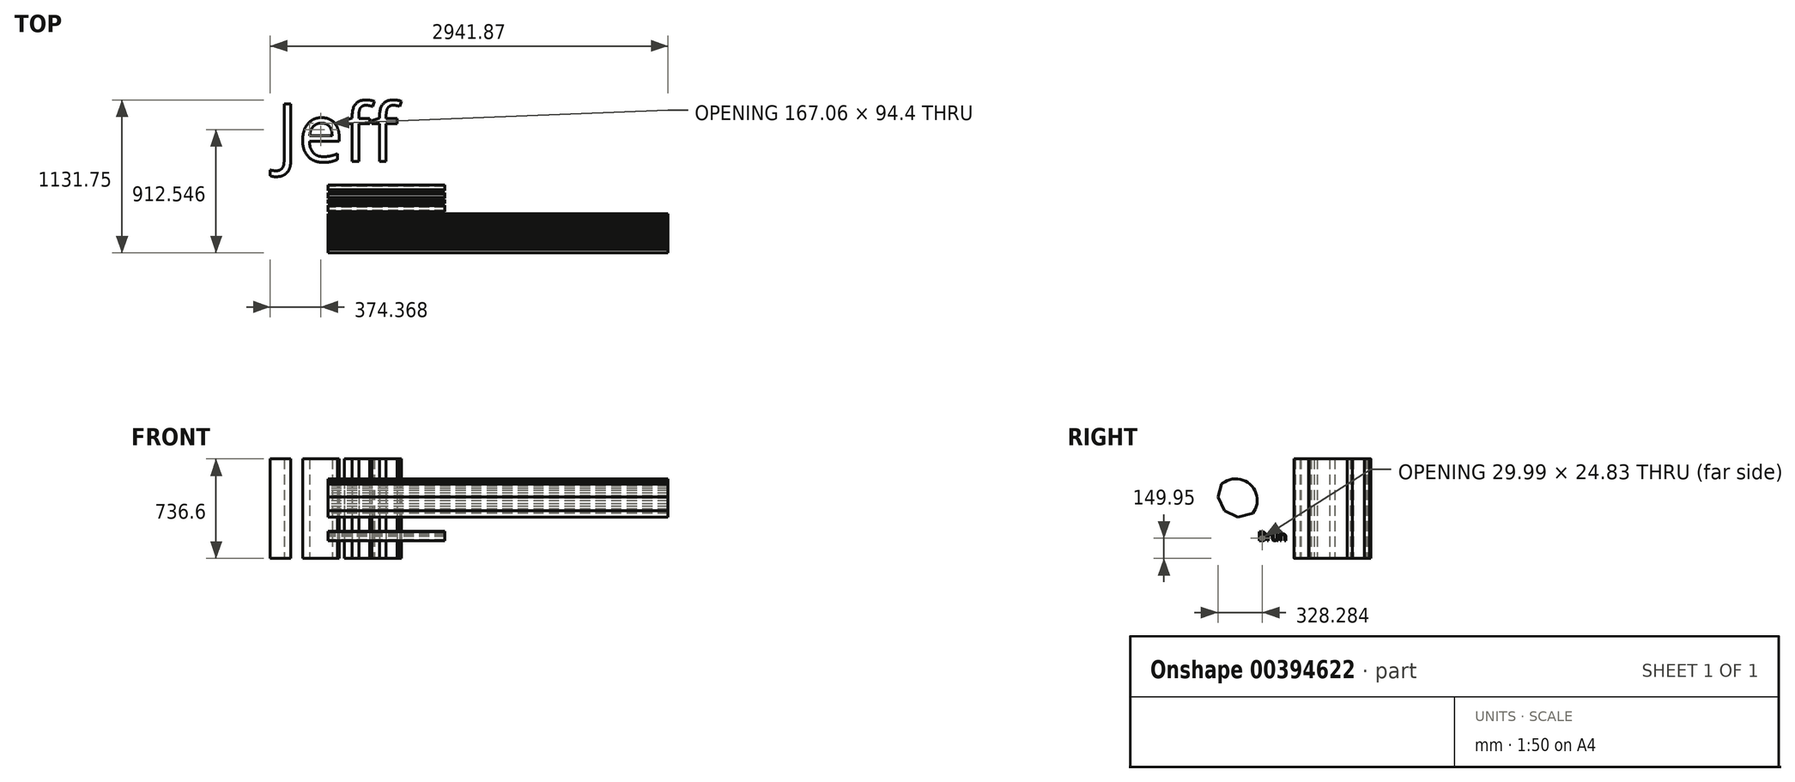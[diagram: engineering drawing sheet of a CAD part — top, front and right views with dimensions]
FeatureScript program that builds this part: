
annotation { "Feature Type Name" : "Feature", "Feature Type Description" : "" }
export const myFeature = defineFeature(function(context is Context, id is Id, definition is map)
    precondition{}
    {
        {
            var Q0;
            Q0=qCreatedBy(makeId("Right.planeOp"),FACE);
            var sketch = newSketch(context, id + "F0", { "sketchPlane" : qUnion([Q0])});
            skCircle(sketch, "E0.cCircle", {"center": v(-776.3, 430.45) * mm, "radius": 159.13 * mm, "construction": true});
            skLineSegment(sketch, "E0.0", {"start": v(-918.13, 358.3) * mm, "end": v(-926.05, 376.64) * mm});
            skLineSegment(sketch, "E0.1", {"start": v(-926.05, 376.64) * mm, "end": v(-931.62, 395.83) * mm});
            skLineSegment(sketch, "E0.2", {"start": v(-931.62, 395.83) * mm, "end": v(-934.73, 415.57) * mm});
            skLineSegment(sketch, "E0.3", {"start": v(-934.73, 415.57) * mm, "end": v(-935.35, 435.54) * mm});
            skLineSegment(sketch, "E0.4", {"start": v(-935.35, 435.54) * mm, "end": v(-933.45, 455.44) * mm});
            skLineSegment(sketch, "E0.5", {"start": v(-933.45, 455.44) * mm, "end": v(-929.08, 474.94) * mm});
            skLineSegment(sketch, "E0.6", {"start": v(-929.08, 474.94) * mm, "end": v(-922.3, 493.73) * mm});
            skLineSegment(sketch, "E0.7", {"start": v(-922.3, 493.73) * mm, "end": v(-913.22, 511.53) * mm});
            skLineSegment(sketch, "E0.8", {"start": v(-913.22, 511.53) * mm, "end": v(-901.98, 528.05) * mm});
            skLineSegment(sketch, "E0.9", {"start": v(-901.98, 528.05) * mm, "end": v(-888.75, 543.04) * mm});
            skLineSegment(sketch, "E0.10", {"start": v(-888.75, 543.04) * mm, "end": v(-873.76, 556.24) * mm});
            skLineSegment(sketch, "E0.11", {"start": v(-873.76, 556.24) * mm, "end": v(-857.22, 567.46) * mm});
            skLineSegment(sketch, "E0.12", {"start": v(-857.22, 567.46) * mm, "end": v(-839.41, 576.53) * mm});
            skLineSegment(sketch, "E0.13", {"start": v(-839.41, 576.53) * mm, "end": v(-820.6, 583.28) * mm});
            skLineSegment(sketch, "E0.14", {"start": v(-820.6, 583.28) * mm, "end": v(-801.1, 587.63) * mm});
            skLineSegment(sketch, "E0.15", {"start": v(-801.1, 587.63) * mm, "end": v(-781.2, 589.5) * mm});
            skLineSegment(sketch, "E0.16", {"start": v(-781.2, 589.5) * mm, "end": v(-761.23, 588.86) * mm});
            skLineSegment(sketch, "E0.17", {"start": v(-761.23, 588.86) * mm, "end": v(-741.5, 585.72) * mm});
            skLineSegment(sketch, "E0.18", {"start": v(-741.5, 585.72) * mm, "end": v(-722.31, 580.14) * mm});
            skLineSegment(sketch, "E0.19", {"start": v(-722.31, 580.14) * mm, "end": v(-703.98, 572.19) * mm});
            skLineSegment(sketch, "E0.20", {"start": v(-703.98, 572.19) * mm, "end": v(-686.78, 562) * mm});
            skLineSegment(sketch, "E0.21", {"start": v(-686.78, 562) * mm, "end": v(-671, 549.75) * mm});
            skLineSegment(sketch, "E0.22", {"start": v(-671, 549.75) * mm, "end": v(-656.88, 535.61) * mm});
            skLineSegment(sketch, "E0.23", {"start": v(-656.88, 535.61) * mm, "end": v(-644.64, 519.81) * mm});
            skLineSegment(sketch, "E0.24", {"start": v(-644.64, 519.81) * mm, "end": v(-634.48, 502.6) * mm});
            skLineSegment(sketch, "E0.25", {"start": v(-634.48, 502.6) * mm, "end": v(-626.55, 484.26) * mm});
            skLineSegment(sketch, "E0.26", {"start": v(-626.55, 484.26) * mm, "end": v(-620.99, 465.07) * mm});
            skLineSegment(sketch, "E0.27", {"start": v(-620.99, 465.07) * mm, "end": v(-617.88, 445.33) * mm});
            skLineSegment(sketch, "E0.28", {"start": v(-617.88, 445.33) * mm, "end": v(-617.26, 425.36) * mm});
            skLineSegment(sketch, "E0.29", {"start": v(-617.26, 425.36) * mm, "end": v(-619.15, 405.46) * mm});
            skLineSegment(sketch, "E0.30", {"start": v(-619.15, 405.46) * mm, "end": v(-623.52, 385.96) * mm});
            skLineSegment(sketch, "E0.31", {"start": v(-623.52, 385.96) * mm, "end": v(-630.3, 367.17) * mm});
            skLineSegment(sketch, "E0.32", {"start": v(-630.3, 367.17) * mm, "end": v(-639.39, 349.37) * mm});
            skLineSegment(sketch, "E0.33", {"start": v(-639.39, 349.37) * mm, "end": v(-650.63, 332.85) * mm});
            skLineSegment(sketch, "E0.34", {"start": v(-650.63, 332.85) * mm, "end": v(-663.85, 317.86) * mm});
            skLineSegment(sketch, "E0.35", {"start": v(-663.85, 317.86) * mm, "end": v(-678.85, 304.66) * mm});
            skLineSegment(sketch, "E0.36", {"start": v(-678.85, 304.66) * mm, "end": v(-695.38, 293.44) * mm});
            skLineSegment(sketch, "E0.37", {"start": v(-695.38, 293.44) * mm, "end": v(-713.2, 284.37) * mm});
            skLineSegment(sketch, "E0.38", {"start": v(-713.2, 284.37) * mm, "end": v(-732, 277.62) * mm});
            skLineSegment(sketch, "E0.39", {"start": v(-732, 277.62) * mm, "end": v(-751.5, 273.27) * mm});
            skLineSegment(sketch, "E0.40", {"start": v(-751.5, 273.27) * mm, "end": v(-771.4, 271.4) * mm});
            skLineSegment(sketch, "E0.41", {"start": v(-771.4, 271.4) * mm, "end": v(-791.37, 272.04) * mm});
            skLineSegment(sketch, "E0.42", {"start": v(-791.37, 272.04) * mm, "end": v(-811.1, 275.18) * mm});
            skLineSegment(sketch, "E0.43", {"start": v(-811.1, 275.18) * mm, "end": v(-830.3, 280.76) * mm});
            skLineSegment(sketch, "E0.44", {"start": v(-830.3, 280.76) * mm, "end": v(-848.63, 288.71) * mm});
            skLineSegment(sketch, "E0.45", {"start": v(-848.63, 288.71) * mm, "end": v(-865.82, 298.9) * mm});
            skLineSegment(sketch, "E0.46", {"start": v(-865.82, 298.9) * mm, "end": v(-881.6, 311.15) * mm});
            skLineSegment(sketch, "E0.47", {"start": v(-881.6, 311.15) * mm, "end": v(-895.73, 325.3) * mm});
            skLineSegment(sketch, "E0.48", {"start": v(-895.73, 325.3) * mm, "end": v(-907.97, 341.09) * mm});
            skLineSegment(sketch, "E0.49", {"start": v(-907.97, 341.09) * mm, "end": v(-918.13, 358.3) * mm});
            skCircle(sketch, "E1.cCircle", {"center": v(-743.96, 467.77) * mm, "radius": 164.06 * mm, "construction": true});
            skLineSegment(sketch, "E1.0", {"start": v(-650.63, 332.85) * mm, "end": v(-759.2, 304.42) * mm});
            skLineSegment(sketch, "E1.1", {"start": v(-759.2, 304.42) * mm, "end": v(-860.63, 352.43) * mm});
            skLineSegment(sketch, "E1.2", {"start": v(-860.63, 352.43) * mm, "end": v(-907.47, 454.41) * mm});
            skLineSegment(sketch, "E1.3", {"start": v(-907.47, 454.41) * mm, "end": v(-877.8, 562.64) * mm});
            skLineSegment(sketch, "E1.4", {"start": v(-877.8, 562.64) * mm, "end": v(-785.51, 626.48) * mm});
            skLineSegment(sketch, "E1.5", {"start": v(-785.51, 626.48) * mm, "end": v(-673.77, 616.06) * mm});
            skLineSegment(sketch, "E1.6", {"start": v(-673.77, 616.06) * mm, "end": v(-594.87, 536.25) * mm});
            skLineSegment(sketch, "E1.7", {"start": v(-594.87, 536.25) * mm, "end": v(-585.73, 424.4) * mm});
            skLineSegment(sketch, "E1.8", {"start": v(-585.73, 424.4) * mm, "end": v(-650.63, 332.85) * mm});
            skSolve(sketch);
        }
        {
            var Q0;
            {var subQ0=sQuery(id+"F0.wireOp",EDGE,"E0.11");Q0=makeQuery(id+"F0.imprint","IMPRINT",FACE,{"disambiguationData":[TD([[makeQuery(id+"F0.imprint","IMPRINT",EDGE,{"derivedFrom":subQ0}),-1.0]])]});}
            extrude(context, id + "F1", {"entities" : qUnion([Q0]), "depth" : 2514.6 * mm});
        }
        {
            var Q0;
            Q0=qCreatedBy(makeId("Top.planeOp"),FACE);
            var sketch = newSketch(context, id + "F2", { "sketchPlane" : qUnion([Q0])});
            skText(sketch, "E2", { "text": "Jeff", "fontName": "OpenSans-Regular.ttf"});
            const initialGuessF2  = {"E2": [-0.38063, -0.2325, 1, 0, 0.42982]};
            skSetInitialGuess(sketch, initialGuessF2);
            skSolve(sketch);
        }
        {
            var Q0;
            Q0 = qSketchRegion(id + "F2", true);
            extrude(context, id + "F3", {"entities" : qUnion([Q0]), "depth" : 736.6 * mm});
        }
        {
            var Q0;
            Q0=qCreatedBy(makeId("Right.planeOp"),FACE);
            var sketch = newSketch(context, id + "F4", { "sketchPlane" : qUnion([Q0])});
            skPoint(sketch, "E3.0", {"position": v(-190.47, 736.6) * mm});
            skText(sketch, "E4", { "text": "Bruh", "fontName": "OpenSans-Regular.ttf"});
            const initialGuessF4  = {"E4": [-0.61101, 0.13096, 1, 0, 0.0669]};
            skSetInitialGuess(sketch, initialGuessF4);
            skSolve(sketch);
        }
        {
            var Q0;
            Q0 = qSketchRegion(id + "F4", true);
            extrude(context, id + "F5", {"entities" : qUnion([Q0]), "depth" : 863.6 * mm});
        }
    });
